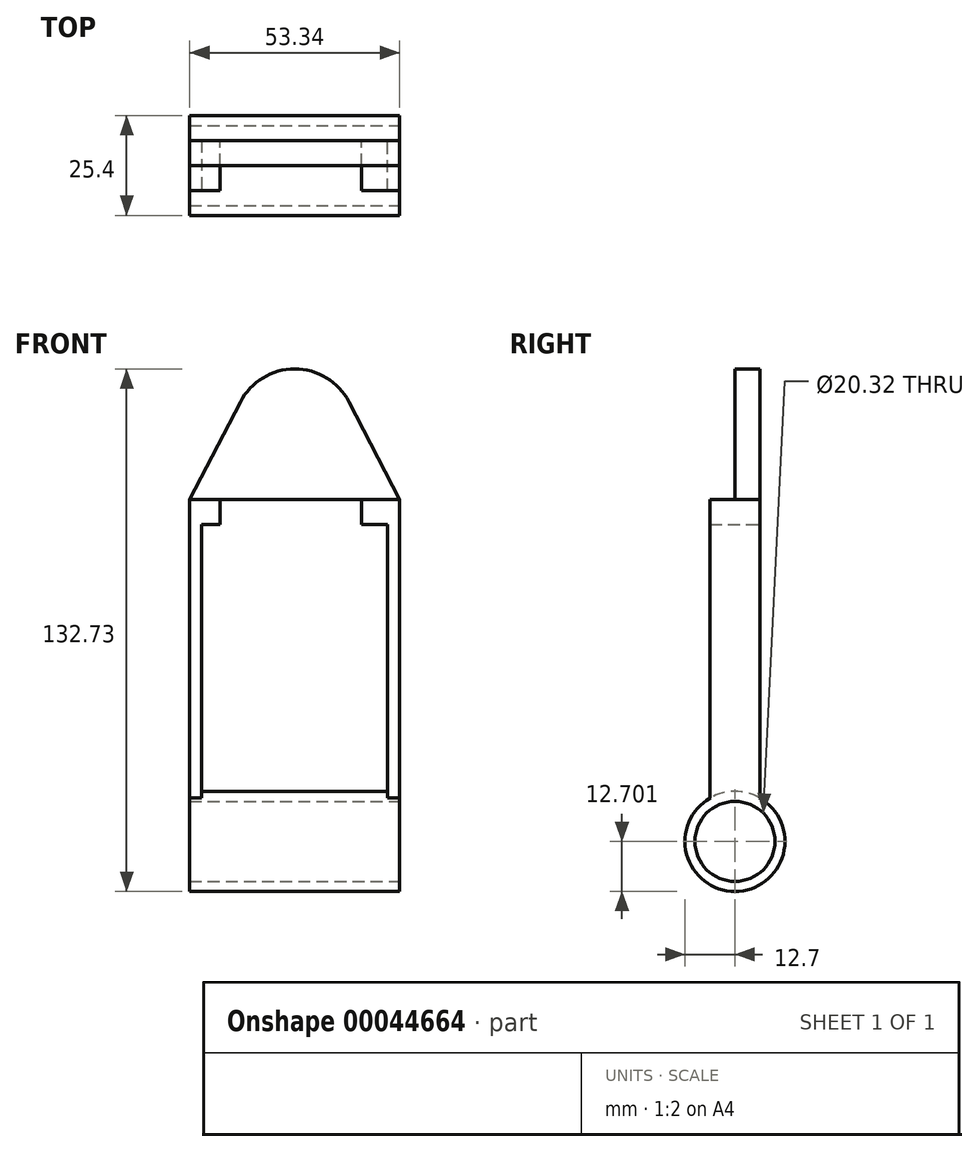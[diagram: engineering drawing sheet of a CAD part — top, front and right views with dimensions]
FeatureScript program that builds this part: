
annotation { "Feature Type Name" : "Feature", "Feature Type Description" : "" }
export const myFeature = defineFeature(function(context is Context, id is Id, definition is map)
    precondition{}
    {
        {
            var Q0;
            Q0=qCreatedBy(makeId("Front.planeOp"),FACE);
            var sketch = newSketch(context, id + "F0", { "sketchPlane" : qUnion([Q0])});
            skArc(sketch, "E0", {"start": v(13.8, 62.4) * mm, "mid": v(0, 70.77) * mm, "end": v(-13.8, 62.4) * mm});
            skLineSegment(sketch, "E1", {"start": v(-13.8, 62.4) * mm, "end": v(-26.67, 37.67) * mm});
            skLineSegment(sketch, "E2", {"start": v(-26.67, 37.67) * mm, "end": v(-26.67, 30.89) * mm});
            skLineSegment(sketch, "E3", {"start": v(-26.67, 30.89) * mm, "end": v(26.67, 30.89) * mm});
            skLineSegment(sketch, "E4", {"start": v(26.67, 30.89) * mm, "end": v(26.67, 37.67) * mm});
            skLineSegment(sketch, "E5", {"start": v(26.67, 37.67) * mm, "end": v(13.8, 62.4) * mm});
            skPoint(sketch, "E6", {"position": v(0, 30.89) * mm});
            skLineSegment(sketch, "E7", {"start": v(26.67, 30.89) * mm, "end": v(26.67, -38.22) * mm});
            skLineSegment(sketch, "E8", {"start": v(26.67, -38.22) * mm, "end": v(-26.67, -38.22) * mm});
            skLineSegment(sketch, "E9", {"start": v(-26.67, -38.22) * mm, "end": v(-26.67, 30.89) * mm});
            skSolve(sketch);
        }
        {
            var Q0;
            Q0 = qSketchRegion(id + "F0", true);
            extrude(context, id + "F1", {"entities" : qUnion([Q0]), "endBound" : BoundingType.SYMMETRIC, "depth" : 12.7 * mm});
        }
        {
            var Q0;
            Q0=makeQuery(id+"F1.opExtrude","CAP_FACE",FACE,{"disambiguationData":[OSD([sQuery(id+"F0.wireOp",EDGE,"E0"),sQuery(id+"F0.wireOp",EDGE,"E1"),sQuery(id+"F0.wireOp",EDGE,"E2"),sQuery(id+"F0.wireOp",EDGE,"E4"),sQuery(id+"F0.wireOp",EDGE,"E5"),sQuery(id+"F0.wireOp",EDGE,"E7"),sQuery(id+"F0.wireOp",EDGE,"E8"),sQuery(id+"F0.wireOp",EDGE,"E9")])],"isStart":true});
            var sketch = newSketch(context, id + "F2", { "sketchPlane" : qUnion([Q0])});
            skLineSegment(sketch, "E10", {"start": v(-23.62, -38.22) * mm, "end": v(-23.62, 31.32) * mm});
            skLineSegment(sketch, "E11", {"start": v(-23.62, 31.32) * mm, "end": v(-16.96, 31.32) * mm});
            skLineSegment(sketch, "E12", {"start": v(-16.96, 31.32) * mm, "end": v(-16.96, 37.67) * mm});
            skLineSegment(sketch, "E13", {"start": v(-16.96, 37.67) * mm, "end": v(-26.67, 37.67) * mm});
            skLineSegment(sketch, "E14", {"start": v(-26.67, 37.67) * mm, "end": v(26.67, 37.67) * mm});
            skLineSegment(sketch, "E15", {"start": v(26.67, 37.67) * mm, "end": v(18.92, 37.67) * mm});
            skLineSegment(sketch, "E16", {"start": v(18.92, 37.67) * mm, "end": v(18.92, 31.32) * mm});
            skLineSegment(sketch, "E17", {"start": v(18.92, 31.32) * mm, "end": v(23.62, 31.32) * mm});
            skLineSegment(sketch, "E18", {"start": v(23.62, 31.32) * mm, "end": v(23.62, -38.22) * mm});
            skLineSegment(sketch, "E19", {"start": v(23.62, -38.22) * mm, "end": v(-23.62, -38.22) * mm});
            skSolve(sketch);
        }
        {
            var Q0;
            Q0 = qSketchRegion(id + "F2", true);
            extrude(context, id + "F3", {"entities" : qUnion([Q0]), "operationType" : NewBodyOperationType.REMOVE, "oppositeDirection" : true, "depth" : 25.4 * mm});
        }
        {
            var Q0;
            Q0=makeQuery(id+"F1.opExtrude","SWEPT_FACE",FACE,{"disambiguationData":[OSD([sQuery(id+"F0.wireOp",EDGE,"E4"),sQuery(id+"F0.wireOp",EDGE,"E7")])]});
            var sketch = newSketch(context, id + "F4", { "sketchPlane" : qUnion([Q0])});
            skLineSegment(sketch, "E20.bottom", {"start": v(-6.35, 37.67) * mm, "end": v(0, 37.67) * mm});
            skLineSegment(sketch, "E20.top", {"start": v(-6.35, 75.77) * mm, "end": v(0, 75.77) * mm});
            skLineSegment(sketch, "E20.left", {"start": v(-6.35, 37.67) * mm, "end": v(-6.35, 75.77) * mm});
            skLineSegment(sketch, "E20.right", {"start": v(0, 37.67) * mm, "end": v(0, 75.77) * mm});
            skSolve(sketch);
        }
        {
            var Q0;
            Q0 = qSketchRegion(id + "F4", true);
            extrude(context, id + "F5", {"entities" : qUnion([Q0]), "operationType" : NewBodyOperationType.REMOVE, "oppositeDirection" : true, "depth" : 63.5 * mm});
        }
        {
            var Q0;
            Q0=makeQuery(id+"F1.opExtrude","SWEPT_FACE",FACE,{"disambiguationData":[OSD([sQuery(id+"F0.wireOp",EDGE,"E4"),sQuery(id+"F0.wireOp",EDGE,"E7")])]});
            var sketch = newSketch(context, id + "F6", { "sketchPlane" : qUnion([Q0])});
            skCircle(sketch, "E21", {"center": v(0, -49.26) * mm, "radius": 12.7 * mm});
            skPoint(sketch, "E21.centerSnap0", {"position": v(0, -38.22) * mm});
            skSolve(sketch);
        }
        {
            var Q0;
            Q0 = qSketchRegion(id + "F6", true);
            extrude(context, id + "F7", {"entities" : qUnion([Q0]), "operationType" : NewBodyOperationType.ADD, "oppositeDirection" : true, "depth" : 53.34 * mm});
        }
        {
            var Q0;
            Q0=makeQuery(id+"F7.boolean.opBoolean","MERGE",FACE,{"derivedFrom":[makeQuery(id+"F1.opExtrude","SWEPT_FACE",FACE,{"disambiguationData":[OSD([sQuery(id+"F0.wireOp",EDGE,"E4"),sQuery(id+"F0.wireOp",EDGE,"E7")])]}),makeQuery(id+"F7.opExtrude","CAP_FACE",FACE,{"disambiguationData":[OSD([sQuery(id+"F6.wireOp",EDGE,"E21")])],"isStart":true})]});
            var sketch = newSketch(context, id + "F8", { "sketchPlane" : qUnion([Q0])});
            skCircle(sketch, "E22", {"center": v(0, -49.26) * mm, "radius": 10.16 * mm});
            skSolve(sketch);
        }
        {
            var Q0;
            Q0 = qSketchRegion(id + "F8", true);
            extrude(context, id + "F9", {"entities" : qUnion([Q0]), "operationType" : NewBodyOperationType.REMOVE, "oppositeDirection" : true, "depth" : 53.34 * mm});
        }
    });
